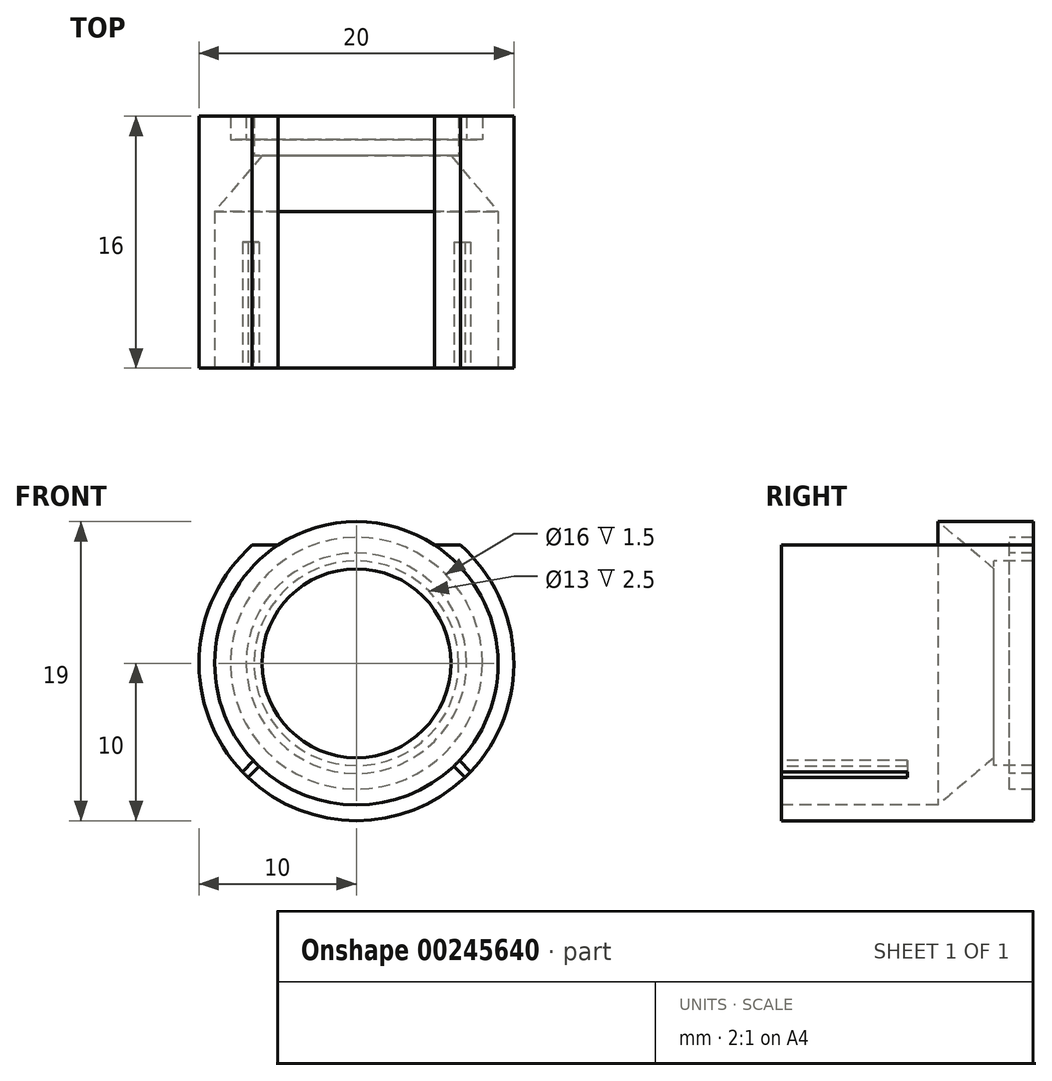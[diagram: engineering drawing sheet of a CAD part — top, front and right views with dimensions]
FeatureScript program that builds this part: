
annotation { "Feature Type Name" : "Feature", "Feature Type Description" : "" }
export const myFeature = defineFeature(function(context is Context, id is Id, definition is map)
    precondition{}
    {
        {
            var Q0;
            Q0=qCreatedBy(makeId("Top.planeOp"),FACE);
            var sketch = newSketch(context, id + "F0", { "sketchPlane" : qUnion([Q0])});
            skLineSegment(sketch, "E0", {"start": v(10, 0) * mm, "end": v(10, 16) * mm});
            skLineSegment(sketch, "E1", {"start": v(10, 16) * mm, "end": v(8, 16) * mm});
            skLineSegment(sketch, "E2", {"start": v(8, 16) * mm, "end": v(8, 14.5) * mm});
            skLineSegment(sketch, "E3", {"start": v(8, 14.5) * mm, "end": v(7, 14.5) * mm});
            skLineSegment(sketch, "E4", {"start": v(7, 14.5) * mm, "end": v(7, 16) * mm});
            skLineSegment(sketch, "E5", {"start": v(7, 16) * mm, "end": v(6.5, 16) * mm});
            skLineSegment(sketch, "E6", {"start": v(6.5, 16) * mm, "end": v(6.5, 13.5) * mm});
            skLineSegment(sketch, "E7", {"start": v(6.5, 13.5) * mm, "end": v(6, 13.5) * mm});
            skLineSegment(sketch, "E8", {"start": v(0, 0) * mm, "end": v(0, 16.02) * mm, "construction": true});
            skLineSegment(sketch, "E9", {"start": v(9, 0) * mm, "end": v(9, 9.95) * mm});
            skLineSegment(sketch, "E10", {"start": v(9, 0) * mm, "end": v(10, 0) * mm});
            skLineSegment(sketch, "E11", {"start": v(6, 13.5) * mm, "end": v(9, 9.95) * mm});
            skSolve(sketch);
        }
        {
            var Q0;
            Q0=makeQuery(id+"F0.imprint","IMPRINT",FACE,{"disambiguationData":[TD([[makeQuery(id+"F0.imprint","IMPRINT",EDGE,{"derivedFrom":sQuery(id+"F0.wireOp",EDGE,"E0")}),1.0]])]});
            var Q1;
            Q1=sQuery(id+"F0.wireOp",EDGE,"E8");
            revolve(context, id + "F1", {"entities" : qUnion([Q0]), "axis" : qUnion([Q1]), "revolveType" : RevolveType.FULL});
        }
        {
            var Q0;
            Q0=makeQuery(id+"F1.opRevolve","SWEPT_FACE",FACE,{"disambiguationData":[OSD([sQuery(id+"F0.wireOp",EDGE,"E10")])]});
            var sketch = newSketch(context, id + "F2", { "sketchPlane" : qUnion([Q0])});
            skLineSegment(sketch, "E12", {"start": v(6.54, -6.18) * mm, "end": v(7.25, -6.9) * mm});
            skLineSegment(sketch, "E13", {"start": v(6.18, -6.54) * mm, "end": v(6.9, -7.25) * mm});
            skLineSegment(sketch, "E14", {"start": v(-6.54, -6.18) * mm, "end": v(-7.25, -6.9) * mm});
            skLineSegment(sketch, "E15", {"start": v(-6.18, -6.54) * mm, "end": v(-6.9, -7.25) * mm});
            skSolve(sketch);
        }
        {
            var Q0;
            {var subQ0=sQuery(id+"F2.wireOp",EDGE,"E14");Q0=makeQuery(id+"F2.imprint","IMPRINT",FACE,{"disambiguationData":[TD([[makeQuery(id+"F2.imprint","IMPRINT",EDGE,{"derivedFrom":subQ0}),1.0]])]});}
            var Q1;
            {var subQ0=sQuery(id+"F2.wireOp",EDGE,"E12");Q1=makeQuery(id+"F2.imprint","IMPRINT",FACE,{"disambiguationData":[TD([[makeQuery(id+"F2.imprint","IMPRINT",EDGE,{"derivedFrom":subQ0}),-1.0]])]});}
            extrude(context, id + "F3", {"entities" : qUnion([Q0, Q1]), "operationType" : NewBodyOperationType.REMOVE, "oppositeDirection" : true, "depth" : 8 * mm});
        }
        {
            var Q0;
            Q0=makeQuery(id+"F3.boolean.opBoolean","SPLIT",FACE,{"disambiguationData":[TD([makeQuery(id+"F3.opExtrude","SWEPT_FACE",FACE,{"disambiguationData":[OSD([sQuery(id+"F2.wireOp",EDGE,"E12")])]})])],"derivedFrom":makeQuery(id+"F1.opRevolve","SWEPT_FACE",FACE,{"disambiguationData":[OSD([sQuery(id+"F0.wireOp",EDGE,"E10")])]})});
            var sketch = newSketch(context, id + "F4", { "sketchPlane" : qUnion([Q0])});
            skLineSegment(sketch, "E16", {"start": v(0, 0) * mm, "end": v(0, 7.5) * mm});
            skLineSegment(sketch, "E17", {"start": v(0, 7.5) * mm, "end": v(6.61, 7.5) * mm});
            skLineSegment(sketch, "E18", {"start": v(6.61, 7.5) * mm, "end": v(-6.61, 7.5) * mm});
            skArc(sketch, "E19", {"start": v(6.61, 7.5) * mm, "mid": v(0, 10) * mm, "end": v(-6.61, 7.5) * mm});
            skSolve(sketch);
        }
        {
            var Q0;
            {var subQ0=sQuery(id+"F4.wireOp",EDGE,"E18");var subQ1=makeQuery(id+"F4.imprint","IMPRINT",VERTEX,{"derivedFrom":subQ0});Q0=makeQuery(id+"F4.imprint","IMPRINT",FACE,{"disambiguationData":[TD([[makeQuery(id+"F4.imprint","IMPRINT",EDGE,{"disambiguationData":[TD([[subQ1,1.0]])],"derivedFrom":subQ0}),-1.0]])]});}
            var Q1;
            {var subQ0=sQuery(id+"F4.wireOp",EDGE,"E19");Q1=makeQuery(id+"F4.imprint","IMPRINT",FACE,{"disambiguationData":[TD([[makeQuery(id+"F4.imprint","IMPRINT",EDGE,{"derivedFrom":subQ0}),1.0]])]});}
            extrude(context, id + "F5", {"entities" : qUnion([Q0, Q1]), "operationType" : NewBodyOperationType.REMOVE, "endBound" : BoundingType.THROUGH_ALL, "oppositeDirection" : true, "depth" : 25 * mm});
        }
    });
